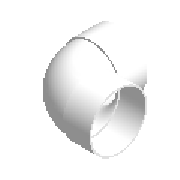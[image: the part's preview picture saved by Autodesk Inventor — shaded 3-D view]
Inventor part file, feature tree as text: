
AUTODESK INVENTOR PART (.ipt)
format: ipt  version: 2023.1 (Build 271208000, 208)  size: 223,232 bytes
history: native  units: mm (DEFAULTED — no unit token found)
features: other x6, sketch x6, extrude x4, sweep x1
ambient origin geometry x8: Origin, YZ Plane, XZ Plane, XY Plane, X Axis, Y Axis, Z Axis, Center Point
bodies: Solid1 (feature_tree)
feature tree (17):
  sweep  "Sweep1"
  extrude  "Extrusion1"  Depth=18.2626mm
  extrude  "Extrusion2"  TaperAngle=0.0deg  [1 undecoded]
  extrude  "Extrusion3"  Depth=21.1328mm
  extrude  "Extrusion4"  Depth=22.3774mm
  other  "Work Axis1"
  other  "Work Point1"
  other  "Work Point2"
  other  "Work Axis2"
  other  "Work Point3"
  other  "Work Point4"
  sketch  "Sketch1"  dims[d0=32.5501mm d1=32.5501mm]
  sketch  "Sketch2"  dims[d2=18.2626mm d3=18.796mm]
  sketch  "Sketch3"  dims[d4=25.9588mm d5=0.0mm]
  sketch  "Sketch4"  dims[d6=32.6136mm d7=21.1328mm]
  sketch  "Sketch5"  dims[d8=0.0mm d9=22.3774mm]
  sketch  "Sketch6"  dims[d10=32.6136mm d11=22.3774mm d12=21.1328mm d13=0.0mm d14=26.8732mm d15=18.2626mm d16=-0.083447mm d17=26.8732mm d18=18.2626mm d19=-0.083447mm d33=0.0mm]
note: 1 required parameter value undecoded (feature->parameter linkage not recoverable at this tier; creation-order binding heuristic only, values carry confidence <= 0.55)
